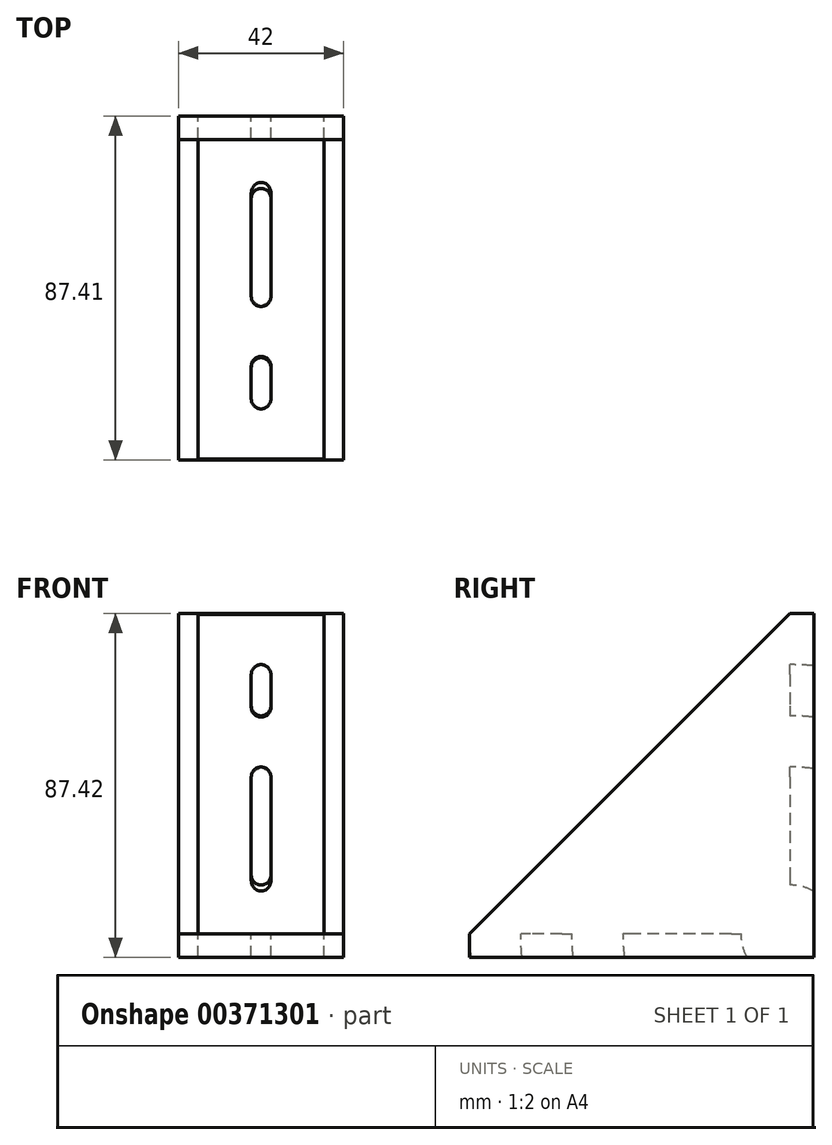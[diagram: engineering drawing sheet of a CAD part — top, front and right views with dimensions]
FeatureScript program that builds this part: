
annotation { "Feature Type Name" : "Feature", "Feature Type Description" : "" }
export const myFeature = defineFeature(function(context is Context, id is Id, definition is map)
    precondition{}
    {
        {
            var Q0;
            Q0=qCreatedBy(makeId("Right.planeOp"),FACE);
            var sketch = newSketch(context, id + "F0", { "sketchPlane" : qUnion([Q0])});
            skLineSegment(sketch, "E0", {"start": v(-1.36, 26.55) * mm, "end": v(-1.36, 111.55) * mm, "construction": true});
            skLineSegment(sketch, "E1", {"start": v(-1.36, 111.55) * mm, "end": v(-4.36, 111.55) * mm});
            skLineSegment(sketch, "E2", {"start": v(-4.36, 111.55) * mm, "end": v(-85.77, 30.13) * mm});
            skLineSegment(sketch, "E3", {"start": v(-85.77, 30.13) * mm, "end": v(-85.77, 26.55) * mm});
            skLineSegment(sketch, "E4", {"start": v(-85.77, 26.55) * mm, "end": v(-1.36, 26.55) * mm});
            skPoint(sketch, "E5.visualSharp", {"position": v(-4.36, 111.55) * mm});
            skLineSegment(sketch, "E5.filletArc", {"start": v(-4.36, 111.55) * mm, "end": v(-4.36, 111.55) * mm});
            skPoint(sketch, "E6.visualSharp", {"position": v(-85.77, 30.13) * mm});
            skLineSegment(sketch, "E6.filletArc", {"start": v(-85.77, 30.13) * mm, "end": v(-85.77, 30.13) * mm});
            skLineSegment(sketch, "E7", {"start": v(-4.36, 111.55) * mm, "end": v(-4.36, 30.13) * mm});
            skLineSegment(sketch, "E8", {"start": v(-4.36, 30.13) * mm, "end": v(-85.77, 30.13) * mm});
            skLineSegment(sketch, "E9", {"start": v(-4.36, 111.55) * mm, "end": v(1.64, 111.55) * mm});
            skLineSegment(sketch, "E10", {"start": v(1.64, 111.55) * mm, "end": v(1.64, 24.13) * mm});
            skLineSegment(sketch, "E11", {"start": v(1.64, 24.13) * mm, "end": v(-85.77, 24.13) * mm});
            skLineSegment(sketch, "E12", {"start": v(-85.77, 24.13) * mm, "end": v(-85.77, 30.13) * mm});
            skSolve(sketch);
        }
        {
            var Q0;
            Q0=qCreatedBy(makeId("Front.planeOp"),FACE);
            var sketch = newSketch(context, id + "F1", { "sketchPlane" : qUnion([Q0])});
            skLineSegment(sketch, "E13", {"start": v(0, 0) * mm, "end": v(5, 0) * mm});
            skLineSegment(sketch, "E14", {"start": v(5, 0) * mm, "end": v(37, 0) * mm});
            skLineSegment(sketch, "E15", {"start": v(37, 0) * mm, "end": v(42, 0) * mm});
            skSolve(sketch);
        }
        {
            var Q0;
            {var subQ2=sQuery(id+"F0.wireOp",EDGE,"E7");Q0=makeQuery(id+"F0.imprint","IMPRINT",FACE,{"disambiguationData":[TD([[makeQuery(id+"F0.imprint","IMPRINT",EDGE,{"derivedFrom":subQ2}),1.0]])]});}
            var Q1;
            Q1=sQuery(id+"F1.wireOp",VERTEX,"E15.end");
            extrude(context, id + "F2", {"entities" : qUnion([Q0]), "endBound" : BoundingType.UP_TO_VERTEX, "endBoundEntityVertex" : qUnion([Q1]), "depth" : 25 * mm});
        }
        {
            var Q0;
            Q0=makeQuery(id+"F0.imprint","IMPRINT",FACE,{"disambiguationData":[TD([[makeQuery(id+"F0.imprint","IMPRINT",EDGE,{"derivedFrom":sQuery(id+"F0.wireOp",EDGE,"E2")}),1.0]])]});
            var Q1;
            Q1=sQuery(id+"F1.wireOp",VERTEX,"E14.start");
            extrude(context, id + "F3", {"entities" : qUnion([Q0]), "operationType" : NewBodyOperationType.ADD, "endBound" : BoundingType.UP_TO_VERTEX, "endBoundEntityVertex" : qUnion([Q1]), "depth" : 25 * mm});
        }
        {
            var Q0;
            Q0=makeQuery(id+"F0.imprint","IMPRINT",FACE,{"disambiguationData":[TD([[makeQuery(id+"F0.imprint","IMPRINT",EDGE,{"derivedFrom":sQuery(id+"F0.wireOp",EDGE,"E2")}),1.0]])]});
            var Q1;
            Q1=sQuery(id+"F1.wireOp",VERTEX,"E15.end");
            var Q2;
            Q2=sQuery(id+"F1.wireOp",VERTEX,"E15.start");
            extrude(context, id + "F4", {"entities" : qUnion([Q0]), "operationType" : NewBodyOperationType.ADD, "endBound" : BoundingType.UP_TO_VERTEX, "endBoundEntityVertex" : qUnion([Q1]), "depth" : 25 * mm, "hasSecondDirection" : true, "secondDirectionBound" : SecondDirectionBoundingType.UP_TO_VERTEX, "secondDirectionOppositeDirection" : false, "secondDirectionBoundEntityVertex" : qUnion([Q2]), "secondDirectionDepth" : 25 * mm});
        }
        {
            var Q0;
            Q0=makeQuery(id+"F2.opExtrude","SWEPT_FACE",FACE,{"disambiguationData":[OSD([sQuery(id+"F0.wireOp",EDGE,"E7")])]});
            var sketch = newSketch(context, id + "F5", { "sketchPlane" : qUnion([Q0])});
            skLineSegment(sketch, "E16", {"start": v(21, 96.05) * mm, "end": v(21, 88.05) * mm, "construction": true});
            skPoint(sketch, "E17", {"position": v(21, 111.55) * mm});
            skLineSegment(sketch, "E18", {"start": v(21, 70.05) * mm, "end": v(21, 45.05) * mm, "construction": true});
            skArc(sketch, "E19.0.startCap", {"start": v(18.5, 96.05) * mm, "mid": v(21, 98.55) * mm, "end": v(23.5, 96.05) * mm});
            skArc(sketch, "E19.0.endCap", {"start": v(23.5, 88.05) * mm, "mid": v(21, 85.55) * mm, "end": v(18.5, 88.05) * mm});
            skLineSegment(sketch, "E19.0.left", {"start": v(23.5, 96.05) * mm, "end": v(23.5, 88.05) * mm});
            skLineSegment(sketch, "E19.0.right", {"start": v(18.5, 96.05) * mm, "end": v(18.5, 88.05) * mm});
            skArc(sketch, "E19.1.startCap", {"start": v(18.5, 70.05) * mm, "mid": v(21, 72.55) * mm, "end": v(23.5, 70.05) * mm});
            skArc(sketch, "E19.1.endCap", {"start": v(23.5, 45.05) * mm, "mid": v(21, 42.55) * mm, "end": v(18.5, 45.05) * mm});
            skLineSegment(sketch, "E19.1.left", {"start": v(23.5, 70.05) * mm, "end": v(23.5, 45.05) * mm});
            skLineSegment(sketch, "E19.1.right", {"start": v(18.5, 70.05) * mm, "end": v(18.5, 45.05) * mm});
            skSolve(sketch);
        }
        {
            var Q0;
            Q0=makeQuery(id+"F5.imprint","IMPRINT",FACE,{"disambiguationData":[TD([[makeQuery(id+"F5.imprint","IMPRINT",EDGE,{"derivedFrom":sQuery(id+"F5.wireOp",EDGE,"E19.0.startCap")}),-1.0]])]});
            var Q1;
            Q1=makeQuery(id+"F5.imprint","IMPRINT",FACE,{"disambiguationData":[TD([[makeQuery(id+"F5.imprint","IMPRINT",EDGE,{"derivedFrom":sQuery(id+"F5.wireOp",EDGE,"E19.1.startCap")}),-1.0]])]});
            var Q2;
            Q2=makeQuery(id+"F2.opExtrude","SWEPT_EDGE",EDGE,{"disambiguationData":[OSD([sQuery(id+"F0.wireOp",EDGE,"E7"),sQuery(id+"F0.wireOp",EDGE,"E8")])]});
            revolve(context, id + "F6", {"operationType" : NewBodyOperationType.REMOVE, "entities" : qUnion([Q0, Q1]), "axis" : qUnion([Q2]), "revolveType" : RevolveType.FULL, "oppositeDirection" : true});
        }
    });
